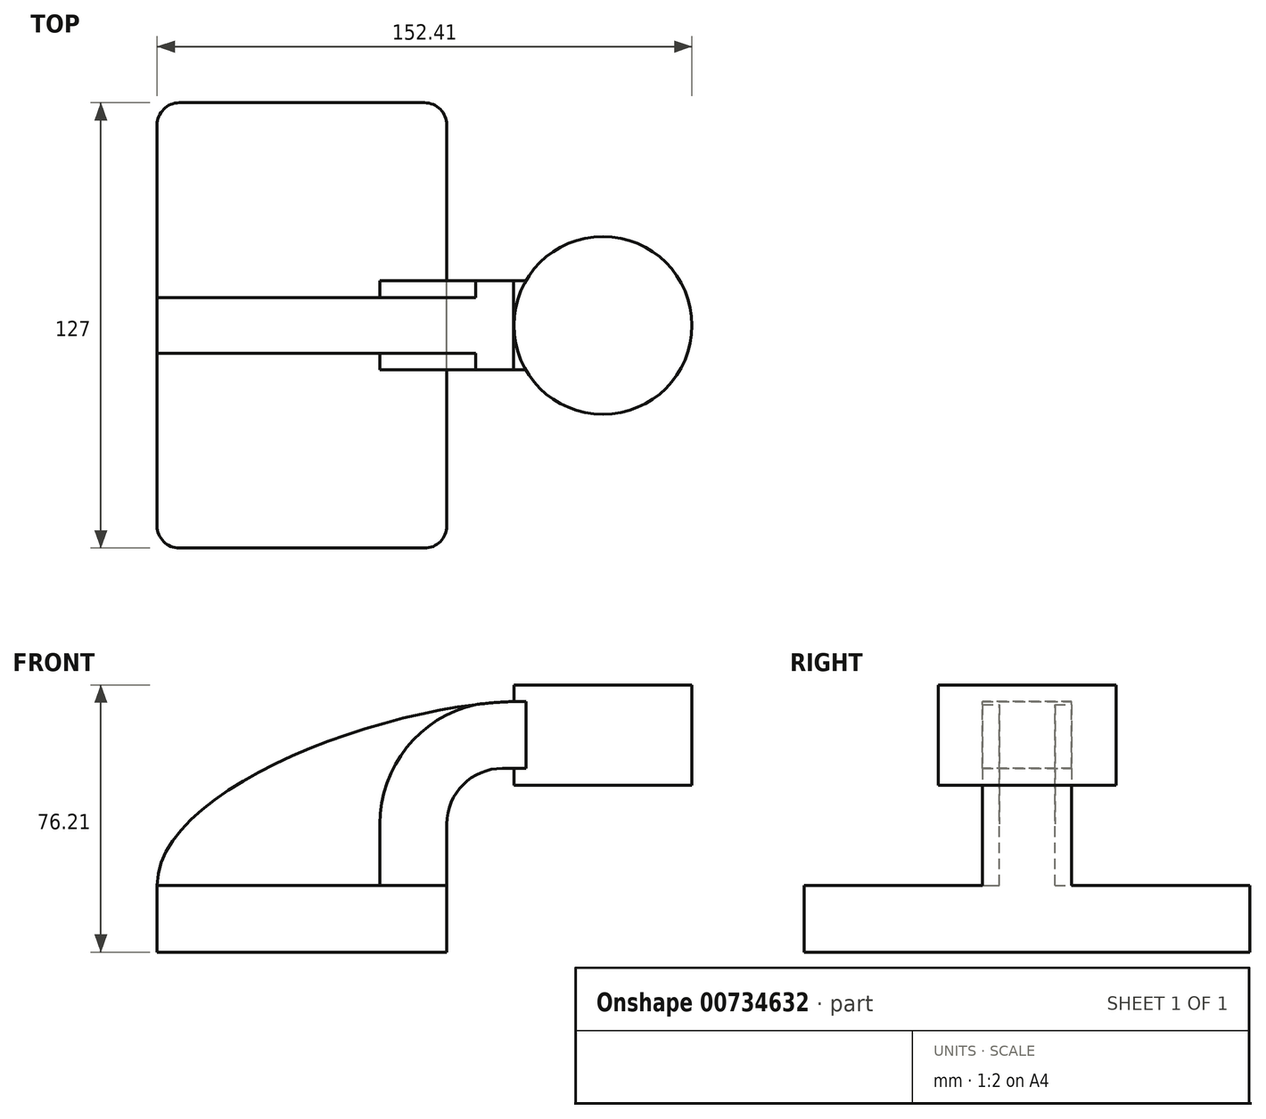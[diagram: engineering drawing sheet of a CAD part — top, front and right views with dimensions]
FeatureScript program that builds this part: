
annotation { "Feature Type Name" : "Feature", "Feature Type Description" : "" }
export const myFeature = defineFeature(function(context is Context, id is Id, definition is map)
    precondition{}
    {
        {
            var Q0;
            Q0=qCreatedBy(makeId("Front.planeOp"),FACE);
            var sketch = newSketch(context, id + "F0", { "sketchPlane" : qUnion([Q0])});
            skLineSegment(sketch, "E0.bottom", {"start": v(41.28, -9.52) * mm, "end": v(-41.27, -9.53) * mm});
            skLineSegment(sketch, "E0.top", {"start": v(41.27, 9.53) * mm, "end": v(-41.28, 9.53) * mm});
            skLineSegment(sketch, "E0.left", {"start": v(41.28, -9.52) * mm, "end": v(41.28, 9.53) * mm});
            skLineSegment(sketch, "E0.right", {"start": v(-41.27, -9.52) * mm, "end": v(-41.28, 9.53) * mm});
            skPoint(sketch, "E0.middle", {"position": v(0, 0) * mm});
            skLineSegment(sketch, "E1.bottom", {"start": v(111.12, 38.1) * mm, "end": v(60.32, 38.1) * mm});
            skLineSegment(sketch, "E1.top", {"start": v(111.12, 66.68) * mm, "end": v(60.32, 66.68) * mm});
            skLineSegment(sketch, "E1.left", {"start": v(111.12, 38.1) * mm, "end": v(111.12, 66.68) * mm});
            skLineSegment(sketch, "E1.right", {"start": v(60.32, 38.1) * mm, "end": v(60.32, 66.68) * mm});
            skPoint(sketch, "E1.middle", {"position": v(85.72, 52.39) * mm});
            skLineSegment(sketch, "E2", {"start": v(41.27, 9.53) * mm, "end": v(41.27, 27) * mm});
            skArc(sketch, "E3", {"start": v(41.27, 27) * mm, "mid": v(45.92, 38.23) * mm, "end": v(57.15, 42.88) * mm});
            skLineSegment(sketch, "E4", {"start": v(57.15, 42.88) * mm, "end": v(85.76, 42.88) * mm});
            skLineSegment(sketch, "E5.0", {"start": v(57.15, 61.93) * mm, "end": v(85.76, 61.93) * mm});
            skArc(sketch, "E5.1", {"start": v(22.23, 27) * mm, "mid": v(32.45, 51.7) * mm, "end": v(57.15, 61.93) * mm});
            skLineSegment(sketch, "E5.2", {"start": v(22.23, 9.53) * mm, "end": v(22.23, 27) * mm});
            skLineSegment(sketch, "E6", {"start": v(85.76, 66.68) * mm, "end": v(85.76, 38.1) * mm});
            skPoint(sketch, "E6.endSnap0", {"position": v(85.72, 38.1) * mm});
            skFitSpline(sketch, "E7", {"points": [v(-41.28, 9.53) * mm, v(60.32, 61.93) * mm], "startDerivative": vector(-0.1, 82.69) * mm, "endDerivative": vector(111.9, 3.28) * mm});
            skSolve(sketch);
        }
        {
            var Q0;
            Q0=makeQuery(id+"F0.imprint","IMPRINT",FACE,{"disambiguationData":[TD([[makeQuery(id+"F0.imprint","IMPRINT",EDGE,{"derivedFrom":sQuery(id+"F0.wireOp",EDGE,"E0.bottom")}),-1.0]])]});
            extrude(context, id + "F1", {"entities" : qUnion([Q0]), "endBound" : BoundingType.SYMMETRIC, "depth" : 127 * mm, "offsetDistance" : 25.4 * mm});
        }
        {
            var Q0;
            {var subQ1=sQuery(id+"F0.wireOp",EDGE,"E2");Q0=makeQuery(id+"F0.imprint","IMPRINT",FACE,{"disambiguationData":[TD([[makeQuery(id+"F0.imprint","IMPRINT",EDGE,{"derivedFrom":subQ1}),1.0]])]});}
            var Q1;
            {var subQ3=sQuery(id+"F0.wireOp",EDGE,"E4");var subQ5=sQuery(id+"F0.wireOp",EDGE,"E6");var subQ6=makeQuery(id+"F0.imprint","INTERSECT",VERTEX,{"derivedFrom":[subQ3,subQ5]});Q1=makeQuery(id+"F0.imprint","IMPRINT",FACE,{"disambiguationData":[TD([[makeQuery(id+"F0.imprint","IMPRINT",EDGE,{"disambiguationData":[TD([[subQ6,1.0]])],"derivedFrom":subQ3}),1.0]])]});}
            extrude(context, id + "F2", {"entities" : qUnion([Q0, Q1]), "operationType" : NewBodyOperationType.ADD, "endBound" : BoundingType.SYMMETRIC, "depth" : 25.4 * mm, "offsetDistance" : 25.4 * mm});
        }
        {
            var Q0;
            {var subQ3=sQuery(id+"F0.wireOp",EDGE,"E5.2");Q0=makeQuery(id+"F0.imprint","IMPRINT",FACE,{"disambiguationData":[TD([[makeQuery(id+"F0.imprint","IMPRINT",EDGE,{"derivedFrom":subQ3}),1.0]])]});}
            extrude(context, id + "F3", {"entities" : qUnion([Q0]), "operationType" : NewBodyOperationType.ADD, "endBound" : BoundingType.SYMMETRIC, "oppositeDirection" : true, "depth" : 15.88 * mm, "offsetDistance" : 25.4 * mm});
        }
        {
            var Q0;
            {var subQ0=sQuery(id+"F0.wireOp",EDGE,"E1.left");Q0=makeQuery(id+"F0.imprint","IMPRINT",FACE,{"disambiguationData":[TD([[makeQuery(id+"F0.imprint","IMPRINT",EDGE,{"derivedFrom":subQ0}),1.0]])]});}
            var Q1;
            Q1=sQuery(id+"F0.wireOp",EDGE,"E6");
            revolve(context, id + "F4", {"operationType" : NewBodyOperationType.ADD, "surfaceOperationType" : NewSurfaceOperationType.NEW, "entities" : qUnion([Q0]), "axis" : qUnion([Q1]), "revolveType" : RevolveType.FULL});
        }
        {
            var Q0;
            Q0=makeQuery(id+"F1.opExtrude","CAP_EDGE",EDGE,{"disambiguationData":[OSD([sQuery(id+"F0.wireOp",EDGE,"E0.left")])],"isStart":false});
            var Q1;
            Q1=makeQuery(id+"F1.opExtrude","CAP_EDGE",EDGE,{"disambiguationData":[OSD([sQuery(id+"F0.wireOp",EDGE,"E0.right")])],"isStart":false});
            var Q2;
            Q2=makeQuery(id+"F1.opExtrude","CAP_EDGE",EDGE,{"disambiguationData":[OSD([sQuery(id+"F0.wireOp",EDGE,"E0.right")])],"isStart":true});
            var Q3;
            Q3=makeQuery(id+"F1.opExtrude","CAP_EDGE",EDGE,{"disambiguationData":[OSD([sQuery(id+"F0.wireOp",EDGE,"E0.left")])],"isStart":true});
            fillet(context, id + "F5", {"entities" : qUnion([Q0, Q1, Q2, Q3]), "radius" : 6.35 * mm, "tangentPropagation" : true, "allowEdgeOverflow" : false});
        }
    });
